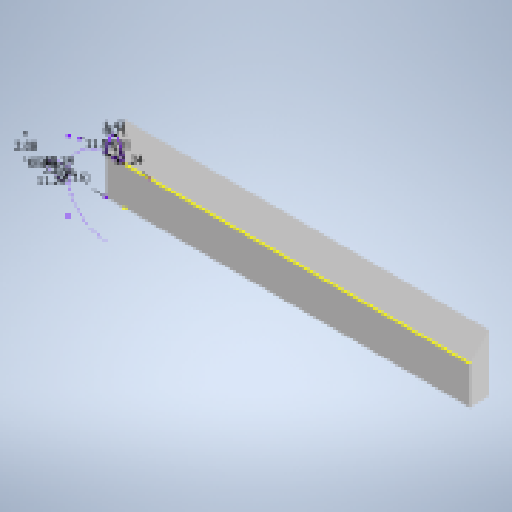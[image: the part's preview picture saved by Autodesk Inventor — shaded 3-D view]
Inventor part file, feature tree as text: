
AUTODESK INVENTOR PART (.ipt)
format: ipt  version: 2023 (Build 270158000, 158)  size: 242,688 bytes
history: native  units: in
note: dims shown in document units (in); Inventor stores cm internally (conversion verified against a paired STEP export)
features: sketch x3, extrude x1, loft x1, pattern_linear x1
ambient origin geometry x8: Origin, YZ Plane, XZ Plane, XY Plane, X Axis, Y Axis, Z Axis, Center Point
bodies: Solid1 (feature_tree)
feature tree (6):
  extrude  "Extrusion1"  Depth=0.1969in
  loft  "Loft1"
  pattern_linear  "Rectangular Pattern1"  Spacing1=0.1638in  [1 undecoded]
  sketch  "Sketch1"  dims[d0=0.5906in d1=0.1969in]
  sketch  "Sketch2"  dims[d2=0.1969in d3=3.5433in d4=0.1969in d5=0.0in d6=0.0in]
  sketch  "Sketch3"  dims[d7=0.1638in d8=0.0819in d9=0.0293in d10=0.0559in d12=0.4425in d13=0.4425in d14=0.2083in d15=0.1638in d16=0.1638in d17=0.0559in d18=0.028in d19=0.2083in d20=0.4425in d21=0.4425in d22=0.1148in d23=0.2295in d24=0.0384in d25=0.0768in d26=0.8315in d27=0.4776in d28=0.4776in d29=0.1148in d30=0.2295in d31=0.0384in d32=0.0768in d33=0.8315in d34=0.4776in d35=0.4776in d36=0.2295in d37=0.2295in d38=0.0768in d39=0.0384in d40=0.2409in d41=0.2409in d42=0.4776in d43=0.4776in d44=0.0in d45=90.0deg d46=0.0in d47=90.0deg d48=4.3307in d50=0.3508in]
note: 1 required parameter value undecoded (feature->parameter linkage not recoverable at this tier; creation-order binding heuristic only, values carry confidence <= 0.55)
